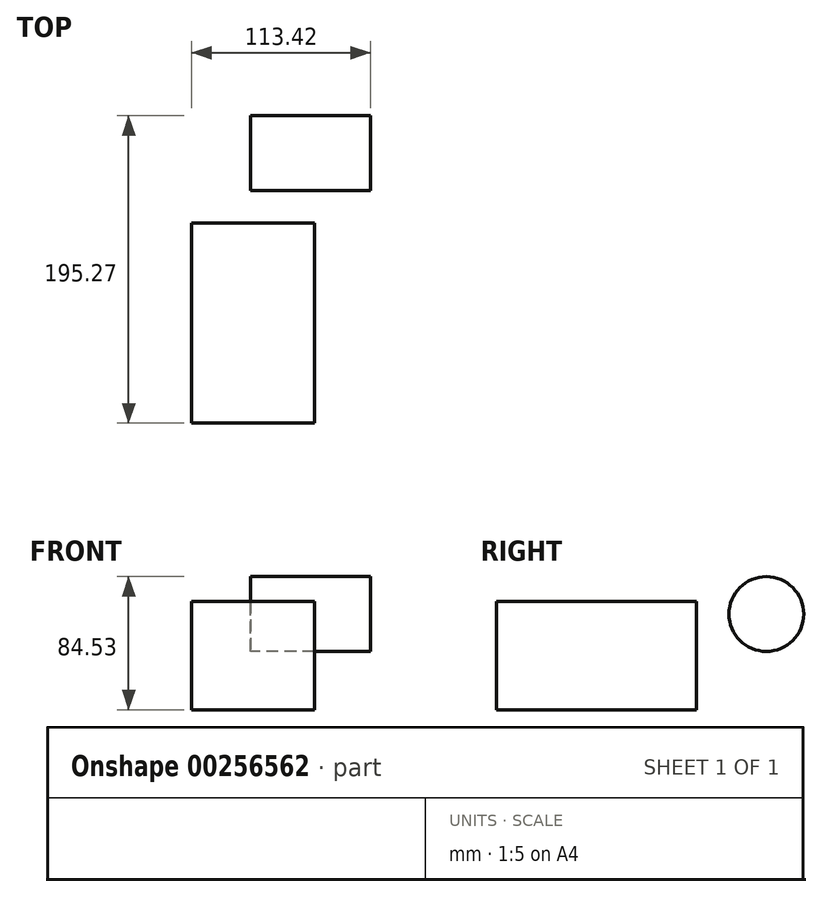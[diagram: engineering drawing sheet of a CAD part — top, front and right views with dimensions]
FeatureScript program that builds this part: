
annotation { "Feature Type Name" : "Feature", "Feature Type Description" : "" }
export const myFeature = defineFeature(function(context is Context, id is Id, definition is map)
    precondition{}
    {
        {
            var Q0;
            Q0=qCreatedBy(makeId("Front.planeOp"),FACE);
            var sketch = newSketch(context, id + "F0", { "sketchPlane" : qUnion([Q0])});
            skLineSegment(sketch, "E0.bottom", {"start": v(40.7, 29.09) * mm, "end": v(-37.22, 29.09) * mm});
            skLineSegment(sketch, "E0.top", {"start": v(40.7, -39.68) * mm, "end": v(-37.22, -39.68) * mm});
            skLineSegment(sketch, "E0.left", {"start": v(40.7, 29.09) * mm, "end": v(40.7, -39.68) * mm});
            skLineSegment(sketch, "E0.right", {"start": v(-37.22, 29.09) * mm, "end": v(-37.22, -39.68) * mm});
            skLineSegment(sketch, "E1.bottom", {"start": v(-106.69, -10.1) * mm, "end": v(-103.94, -10.1) * mm});
            skLineSegment(sketch, "E1.top", {"start": v(-106.69, -3.17) * mm, "end": v(-103.94, -3.17) * mm});
            skLineSegment(sketch, "E1.left", {"start": v(-106.69, -10.1) * mm, "end": v(-106.69, -3.17) * mm});
            skLineSegment(sketch, "E1.right", {"start": v(-103.94, -10.1) * mm, "end": v(-103.94, -3.17) * mm});
            skSolve(sketch);
        }
        {
            var Q0;
            Q0=makeQuery(id+"F0.imprint","IMPRINT",FACE,{"disambiguationData":[TD([[makeQuery(id+"F0.imprint","IMPRINT",EDGE,{"derivedFrom":sQuery(id+"F0.wireOp",EDGE,"E0.bottom")}),1.0]])]});
            extrude(context, id + "F1", {"entities" : qUnion([Q0]), "depth" : 127 * mm});
        }
        {
            var Q0;
            Q0=qCreatedBy(makeId("Right.planeOp"),FACE);
            var sketch = newSketch(context, id + "F2", { "sketchPlane" : qUnion([Q0])});
            skCircle(sketch, "E2", {"center": v(44.54, 21.1) * mm, "radius": 23.74 * mm});
            skSolve(sketch);
        }
        {
            var Q0;
            Q0=makeQuery(id+"F2.imprint","IMPRINT",FACE,{"disambiguationData":[TD([[makeQuery(id+"F2.imprint","IMPRINT",EDGE,{"derivedFrom":sQuery(id+"F2.wireOp",EDGE,"E2")}),1.0]])]});
            extrude(context, id + "F3", {"entities" : qUnion([Q0]), "depth" : 76.2 * mm});
        }
    });
